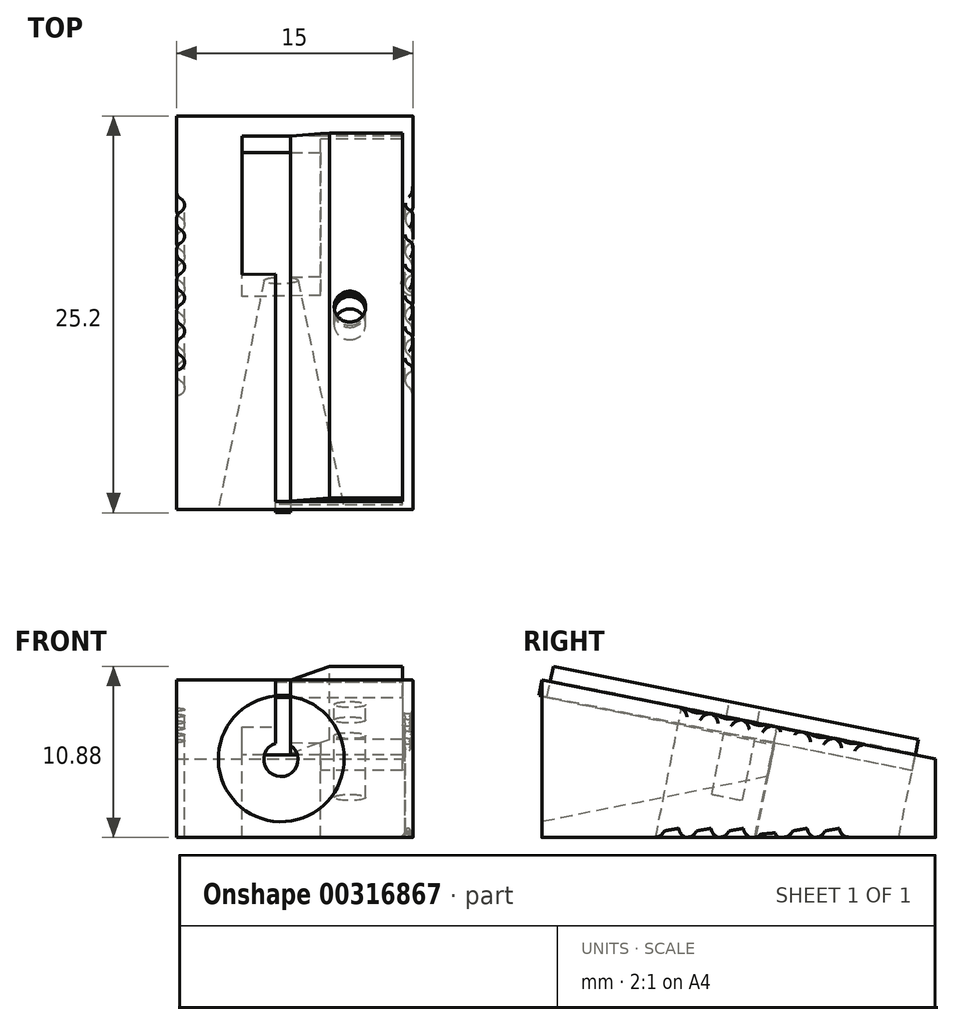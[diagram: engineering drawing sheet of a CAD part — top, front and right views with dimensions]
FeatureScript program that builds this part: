
annotation { "Feature Type Name" : "Feature", "Feature Type Description" : "" }
export const myFeature = defineFeature(function(context is Context, id is Id, definition is map)
    precondition{}
    {
        {
            var Q0;
            Q0=qCreatedBy(makeId("Front.planeOp"),FACE);
            cPlane(context, id + "F0", {"entities" : qUnion([Q0]), "cplaneType" : CPlaneType.OFFSET, "offset" : 10 * mm, "width" : 150 * mm, "height" : 150 * mm});
        }
        {
            var Q0;
            Q0=qCreatedBy(makeId("Front.planeOp"),FACE);
            var sketch = newSketch(context, id + "F1", { "sketchPlane" : qUnion([Q0])});
            skLineSegment(sketch, "E0.bottom", {"start": v(7.5, 5) * mm, "end": v(-7.5, 5) * mm});
            skLineSegment(sketch, "E0.top", {"start": v(7.5, -5) * mm, "end": v(-7.5, -5) * mm});
            skLineSegment(sketch, "E0.left", {"start": v(7.5, 5) * mm, "end": v(7.5, -5) * mm});
            skLineSegment(sketch, "E0.right", {"start": v(-7.5, 5) * mm, "end": v(-7.5, -5) * mm});
            skPoint(sketch, "E0.middle", {"position": v(0, 0) * mm});
            skSolve(sketch);
        }
        {
            var Q0;
            Q0=makeQuery(id+"F1.imprint","IMPRINT",FACE,{"disambiguationData":[TD([[makeQuery(id+"F1.imprint","IMPRINT",EDGE,{"derivedFrom":sQuery(id+"F1.wireOp",EDGE,"E0.bottom")}),1.0]])]});
            extrude(context, id + "F2", {"entities" : qUnion([Q0]), "depth" : 25 * mm});
        }
        {
            var Q0;
            Q0=makeQuery(id+"F2.opExtrude","SWEPT_FACE",FACE,{"disambiguationData":[OSD([sQuery(id+"F1.wireOp",EDGE,"E0.left")])]});
            var sketch = newSketch(context, id + "F3", { "sketchPlane" : qUnion([Q0])});
            skLineSegment(sketch, "E1", {"start": v(0, -5) * mm, "end": v(0, 0) * mm, "construction": true});
            skLineSegment(sketch, "E2", {"start": v(0, 0) * mm, "end": v(-25, 5) * mm, "construction": true});
            skLineSegment(sketch, "E3", {"start": v(-25, 5) * mm, "end": v(0, 0) * mm});
            skLineSegment(sketch, "E4", {"start": v(0, 0) * mm, "end": v(0, 5) * mm});
            skLineSegment(sketch, "E5", {"start": v(0, 5) * mm, "end": v(-25, 5) * mm});
            skSolve(sketch);
        }
        {
            var Q0;
            Q0 = qSketchRegion(id + "F3", true);
            extrude(context, id + "F4", {"entities" : qUnion([Q0]), "operationType" : NewBodyOperationType.REMOVE, "oppositeDirection" : true, "depth" : 25 * mm});
        }
        {
            var Q0;
            Q0=makeQuery(id+"F2.opExtrude","CAP_FACE",FACE,{"disambiguationData":[OSD([sQuery(id+"F1.wireOp",EDGE,"E0.bottom"),sQuery(id+"F1.wireOp",EDGE,"E0.top"),sQuery(id+"F1.wireOp",EDGE,"E0.left"),sQuery(id+"F1.wireOp",EDGE,"E0.right")])],"isStart":false});
            var sketch = newSketch(context, id + "F5", { "sketchPlane" : qUnion([Q0])});
            skCircle(sketch, "E6", {"center": v(-0.86, 0) * mm, "radius": 4 * mm});
            skSolve(sketch);
        }
        {
            var Q0;
            Q0=qCreatedBy(id+"F0.planeOp",FACE);
            var sketch = newSketch(context, id + "F6", { "sketchPlane" : qUnion([Q0])});
            skCircle(sketch, "E7", {"center": v(-0.87, 0) * mm, "radius": 1 * mm});
            skSolve(sketch);
        }
        {
            var Q0;
            Q0=makeQuery(id+"F4.boolean.opBoolean","COPY",FACE,{"derivedFrom":makeQuery(id+"F4.opExtrude","SWEPT_FACE",FACE,{"disambiguationData":[OSD([sQuery(id+"F3.wireOp",EDGE,"E3")])]})});
            var sketch = newSketch(context, id + "F7", { "sketchPlane" : qUnion([Q0])});
            skLineSegment(sketch, "E8", {"start": v(1.64, -10.2) * mm, "end": v(1.64, -1.3) * mm});
            skLineSegment(sketch, "E9", {"start": v(1.64, -1.3) * mm, "end": v(-3.36, -1.3) * mm});
            skLineSegment(sketch, "E10", {"start": v(-3.36, -1.3) * mm, "end": v(-3.36, -10.27) * mm});
            skLineSegment(sketch, "E11", {"start": v(-3.36, -10.27) * mm, "end": v(1.64, -10.2) * mm});
            skSolve(sketch);
        }
        {
            var Q1;
            Q1=makeQuery(id+"F5.imprint","IMPRINT",FACE,{"disambiguationData":[TD([[makeQuery(id+"F5.imprint","IMPRINT",EDGE,{"derivedFrom":sQuery(id+"F5.wireOp",EDGE,"E6")}),1.0]])]});
            var Q2;
            Q2=makeQuery(id+"F6.imprint","IMPRINT",FACE,{"disambiguationData":[TD([[makeQuery(id+"F6.imprint","IMPRINT",EDGE,{"derivedFrom":sQuery(id+"F6.wireOp",EDGE,"E7")}),1.0]])]});
            loft(context, id + "F8", {"operationType" : NewBodyOperationType.REMOVE, "sheetProfilesArray" : [{ "sheetProfileEntities" : qUnion([Q1]) }, { "sheetProfileEntities" : qUnion([Q2]) }]});
        }
        {
            var Q0;
            Q0=makeQuery(id+"F7.imprint","IMPRINT",FACE,{"disambiguationData":[TD([[makeQuery(id+"F7.imprint","IMPRINT",EDGE,{"derivedFrom":sQuery(id+"F7.wireOp",EDGE,"E8")}),1.0]])]});
            extrude(context, id + "F9", {"entities" : qUnion([Q0]), "operationType" : NewBodyOperationType.REMOVE, "oppositeDirection" : true, "depth" : 25 * mm});
        }
        {
            var Q0;
            Q0=qCreatedBy(makeId("Top.planeOp"),FACE);
            var sketch = newSketch(context, id + "F10", { "sketchPlane" : qUnion([Q0])});
            skLineSegment(sketch, "E12.bottom", {"start": v(-0.26, -10.02) * mm, "end": v(-1.23, -10.02) * mm});
            skLineSegment(sketch, "E12.top", {"start": v(-0.26, -26.35) * mm, "end": v(-1.23, -26.35) * mm});
            skLineSegment(sketch, "E12.left", {"start": v(-0.26, -10.02) * mm, "end": v(-0.26, -26.35) * mm});
            skLineSegment(sketch, "E12.right", {"start": v(-1.23, -10.02) * mm, "end": v(-1.23, -26.35) * mm});
            skSolve(sketch);
        }
        {
            var Q0;
            Q0=makeQuery(id+"F10.imprint","IMPRINT",FACE,{"disambiguationData":[TD([[makeQuery(id+"F10.imprint","IMPRINT",EDGE,{"derivedFrom":sQuery(id+"F10.wireOp",EDGE,"E12.bottom")}),1.0]])]});
            extrude(context, id + "F11", {"entities" : qUnion([Q0]), "operationType" : NewBodyOperationType.REMOVE, "depth" : 25 * mm});
        }
        {
            var Q0;
            Q0=makeQuery(id+"F4.boolean.opBoolean","COPY",FACE,{"derivedFrom":makeQuery(id+"F4.opExtrude","SWEPT_FACE",FACE,{"disambiguationData":[OSD([sQuery(id+"F3.wireOp",EDGE,"E3")])]})});
            var sketch = newSketch(context, id + "F12", { "sketchPlane" : qUnion([Q0])});
            skPoint(sketch, "E13.endSnap0", {"position": v(7.5, -12.75) * mm});
            skCircle(sketch, "E14", {"center": v(3.5, -12.5) * mm, "radius": 1 * mm});
            skSolve(sketch);
        }
        {
            var Q0;
            Q0=makeQuery(id+"F12.imprint","IMPRINT",FACE,{"disambiguationData":[TD([[makeQuery(id+"F12.imprint","IMPRINT",EDGE,{"derivedFrom":sQuery(id+"F12.wireOp",EDGE,"E14")}),1.0]])]});
            var Q1;
            Q1=sQuery(id+"F12.wireOp",EDGE,"E14");
            extrude(context, id + "F13", {"entities" : qUnion([Q0]), "operationType" : NewBodyOperationType.REMOVE, "surfaceEntities" : qUnion([Q1]), "oppositeDirection" : true, "depth" : 5 * mm});
        }
        {
            var Q0;
            Q0=makeQuery(id+"F4.boolean.opBoolean","COPY",FACE,{"derivedFrom":makeQuery(id+"F4.opExtrude","SWEPT_FACE",FACE,{"disambiguationData":[OSD([sQuery(id+"F3.wireOp",EDGE,"E3")])]})});
            var sketch = newSketch(context, id + "F14", { "sketchPlane" : qUnion([Q0])});
            skLineSegment(sketch, "E15", {"start": v(-0.26, -24.96) * mm, "end": v(6.83, -24.96) * mm});
            skLineSegment(sketch, "E16", {"start": v(6.83, -24.96) * mm, "end": v(6.83, -1.3) * mm});
            skLineSegment(sketch, "E17", {"start": v(6.83, -1.3) * mm, "end": v(1.64, -1.3) * mm});
            skLineSegment(sketch, "E18", {"start": v(1.64, -1.3) * mm, "end": v(1.64, -10.2) * mm});
            skLineSegment(sketch, "E19", {"start": v(1.64, -10.2) * mm, "end": v(-0.26, -10.23) * mm});
            skLineSegment(sketch, "E20", {"start": v(-0.26, -10.23) * mm, "end": v(-0.26, -24.96) * mm});
            skSolve(sketch);
        }
        {
            var Q0;
            Q0=makeQuery(id+"F14.imprint","IMPRINT",FACE,{"disambiguationData":[TD([[makeQuery(id+"F14.imprint","IMPRINT",EDGE,{"derivedFrom":sQuery(id+"F14.wireOp",EDGE,"E15")}),1.0]])]});
            extrude(context, id + "F15", {"entities" : qUnion([Q0]), "operationType" : NewBodyOperationType.REMOVE, "oppositeDirection" : true, "depth" : 1 * mm});
        }
        {
            var Q0;
            Q0=makeQuery(id+"F4.boolean.opBoolean","COPY",FACE,{"derivedFrom":makeQuery(id+"F4.opExtrude","SWEPT_FACE",FACE,{"disambiguationData":[OSD([sQuery(id+"F3.wireOp",EDGE,"E3")])]})});
            var sketch = newSketch(context, id + "F16", { "sketchPlane" : qUnion([Q0])});
            skLineSegment(sketch, "E21", {"start": v(-0.26, -24.96) * mm, "end": v(-1.23, -24.96) * mm});
            skLineSegment(sketch, "E22", {"start": v(-1.23, -24.96) * mm, "end": v(-1.23, -25.5) * mm});
            skLineSegment(sketch, "E23", {"start": v(-1.23, -25.5) * mm, "end": v(-0.26, -25.5) * mm});
            skLineSegment(sketch, "E24", {"start": v(-0.26, -25.5) * mm, "end": v(-0.26, -24.96) * mm});
            skSolve(sketch);
        }
        {
            var Q0;
            Q0=makeQuery(id+"F16.imprint","IMPRINT",FACE,{"disambiguationData":[TD([[makeQuery(id+"F16.imprint","IMPRINT",EDGE,{"derivedFrom":sQuery(id+"F16.wireOp",EDGE,"E21")}),1.0]])]});
            extrude(context, id + "F17", {"entities" : qUnion([Q0]), "operationType" : NewBodyOperationType.ADD, "oppositeDirection" : true, "depth" : 1 * mm});
        }
        {
            var Q0;
            Q0=makeQuery(id+"F17.boolean.opBoolean","MERGE",FACE,{"derivedFrom":[makeQuery(id+"F4.boolean.opBoolean","COPY",FACE,{"derivedFrom":makeQuery(id+"F4.opExtrude","SWEPT_FACE",FACE,{"disambiguationData":[OSD([sQuery(id+"F3.wireOp",EDGE,"E3")])]})}),makeQuery(id+"F17.opExtrude","CAP_FACE",FACE,{"disambiguationData":[OSD([sQuery(id+"F16.wireOp",EDGE,"E21"),sQuery(id+"F16.wireOp",EDGE,"E22"),sQuery(id+"F16.wireOp",EDGE,"E23"),sQuery(id+"F16.wireOp",EDGE,"E24")])],"isStart":true})]});
            var sketch = newSketch(context, id + "F18", { "sketchPlane" : qUnion([Q0])});
            skLineSegment(sketch, "E25.bottom", {"start": v(6.83, -1.3) * mm, "end": v(-0.27, -1.3) * mm});
            skLineSegment(sketch, "E25.top", {"start": v(6.83, -24.96) * mm, "end": v(-0.27, -24.96) * mm});
            skLineSegment(sketch, "E25.left", {"start": v(6.83, -1.3) * mm, "end": v(6.83, -24.96) * mm});
            skLineSegment(sketch, "E25.right", {"start": v(-0.27, -1.3) * mm, "end": v(-0.27, -24.96) * mm});
            skSolve(sketch);
        }
        {
            var Q0;
            {var subQ1=sQuery(id+"F18.wireOp",EDGE,"E25.top");Q0=makeQuery(id+"F18.imprint","IMPRINT",FACE,{"disambiguationData":[TD([[makeQuery(id+"F18.imprint","IMPRINT",EDGE,{"derivedFrom":subQ1}),1.0]])]});}
            extrude(context, id + "F19", {"entities" : qUnion([Q0]), "depth" : 1 * mm});
        }
        {
            var Q0;
            Q0=makeQuery(id+"F19.opExtrude","CAP_FACE",FACE,{"disambiguationData":[OSD([sQuery(id+"F7.wireOp",EDGE,"E9"),sQuery(id+"F14.wireOp",EDGE,"E17"),sQuery(id+"F18.wireOp",EDGE,"E25.top"),sQuery(id+"F18.wireOp",EDGE,"E25.left"),sQuery(id+"F18.wireOp",EDGE,"E25.right")])],"isStart":false});
            var sketch = newSketch(context, id + "F20", { "sketchPlane" : qUnion([Q0])});
            skCircle(sketch, "E26", {"center": v(3.5, -12.55) * mm, "radius": 1 * mm});
            skSolve(sketch);
        }
        {
            var Q0;
            Q0 = qSketchRegion(id + "F20", true);
            var Q1;
            Q1=sQuery(id+"F20.wireOp",EDGE,"E26");
            extrude(context, id + "F21", {"entities" : qUnion([Q0]), "operationType" : NewBodyOperationType.REMOVE, "surfaceEntities" : qUnion([Q1]), "oppositeDirection" : true, "depth" : 1 * mm});
        }
        {
            var Q0;
            Q0=makeQuery(id+"F19.opExtrude","CAP_EDGE",EDGE,{"disambiguationData":[OSD([sQuery(id+"F18.wireOp",EDGE,"E25.right")])],"isStart":false});
            chamfer(context, id + "F22", {"entities" : qUnion([Q0]), "chamferType" : ChamferType.OFFSET_ANGLE, "width" : 0.9 * mm, "oppositeDirection" : true, "angle" : 70 * degree});
        }
        {
            var Q0;
            {var subQ12=sQuery(id+"F18.wireOp",EDGE,"E25.bottom");Q0=makeQuery(id+"F18.imprint","IMPRINT",FACE,{"disambiguationData":[TD([[makeQuery(id+"F18.imprint","IMPRINT",EDGE,{"derivedFrom":subQ12}),-1.0]])]});}
            var sketch = newSketch(context, id + "F23", { "sketchPlane" : qUnion([Q0])});
            skLineSegment(sketch, "E27", {"start": v(-7.5, -4.67) * mm, "end": v(-7.5, -19.77) * mm});
            skArc(sketch, "E28", {"start": v(-7.5, -6.28) * mm, "mid": v(-7, -5.78) * mm, "end": v(-7.5, -5.28) * mm});
            skArc(sketch, "E29", {"start": v(-7.5, -6.28) * mm, "mid": v(-8, -6.78) * mm, "end": v(-7.5, -7.28) * mm});
            skArc(sketch, "E30", {"start": v(-7.5, -8.29) * mm, "mid": v(-7, -7.79) * mm, "end": v(-7.5, -7.29) * mm});
            skArc(sketch, "E31", {"start": v(-7.5, -8.3) * mm, "mid": v(-8, -8.8) * mm, "end": v(-7.5, -9.3) * mm});
            skArc(sketch, "E32", {"start": v(-7.5, -10.27) * mm, "mid": v(-7, -9.77) * mm, "end": v(-7.5, -9.27) * mm});
            skArc(sketch, "E33", {"start": v(-7.5, -10.28) * mm, "mid": v(-8, -10.78) * mm, "end": v(-7.5, -11.28) * mm});
            skArc(sketch, "E34", {"start": v(-7.5, -12.28) * mm, "mid": v(-7, -11.78) * mm, "end": v(-7.5, -11.28) * mm});
            skArc(sketch, "E35", {"start": v(-7.5, -12.29) * mm, "mid": v(-8, -12.79) * mm, "end": v(-7.5, -13.29) * mm});
            skArc(sketch, "E36", {"start": v(-7.5, -14.44) * mm, "mid": v(-7, -13.94) * mm, "end": v(-7.5, -13.44) * mm});
            skArc(sketch, "E37", {"start": v(-7.5, -14.45) * mm, "mid": v(-8, -14.95) * mm, "end": v(-7.5, -15.45) * mm});
            skArc(sketch, "E38", {"start": v(-7.5, -16.45) * mm, "mid": v(-7, -15.95) * mm, "end": v(-7.5, -15.45) * mm});
            skArc(sketch, "E39", {"start": v(-7.5, -16.46) * mm, "mid": v(-8, -16.96) * mm, "end": v(-7.5, -17.46) * mm});
            skSolve(sketch);
        }
        {
            var Q0;
            Q0 = qSketchRegion(id + "F23", true);
            extrude(context, id + "F24", {"entities" : qUnion([Q0]), "operationType" : NewBodyOperationType.REMOVE, "oppositeDirection" : true, "depth" : 25 * mm});
        }
        {
            var Q0;
            {var subQ12=sQuery(id+"F18.wireOp",EDGE,"E25.bottom");Q0=makeQuery(id+"F18.imprint","IMPRINT",FACE,{"disambiguationData":[TD([[makeQuery(id+"F18.imprint","IMPRINT",EDGE,{"derivedFrom":subQ12}),-1.0]])]});}
            var sketch = newSketch(context, id + "F25", { "sketchPlane" : qUnion([Q0])});
            skLineSegment(sketch, "E40", {"start": v(-7.65, -16.68) * mm, "end": v(7.4, -16.68) * mm, "construction": true});
            skLineSegment(sketch, "E41", {"start": v(7.5, -5.06) * mm, "end": v(7.5, -16.68) * mm});
            skArc(sketch, "E42", {"start": v(7.5, -5.06) * mm, "mid": v(7.02, -5.56) * mm, "end": v(7.5, -6.06) * mm});
            skArc(sketch, "E43", {"start": v(7.5, -7.06) * mm, "mid": v(8, -6.56) * mm, "end": v(7.5, -6.06) * mm});
            skArc(sketch, "E44", {"start": v(7.5, -7.07) * mm, "mid": v(7, -7.57) * mm, "end": v(7.5, -8.07) * mm});
            skArc(sketch, "E45", {"start": v(7.5, -9.02) * mm, "mid": v(8, -8.52) * mm, "end": v(7.5, -8.02) * mm});
            skArc(sketch, "E46", {"start": v(7.5, -9.03) * mm, "mid": v(7, -9.53) * mm, "end": v(7.5, -10.03) * mm});
            skArc(sketch, "E47", {"start": v(7.5, -11.03) * mm, "mid": v(8, -10.53) * mm, "end": v(7.5, -10.03) * mm});
            skArc(sketch, "E48", {"start": v(7.5, -11.04) * mm, "mid": v(7, -11.54) * mm, "end": v(7.5, -12.04) * mm});
            skArc(sketch, "E49", {"start": v(7.5, -13.05) * mm, "mid": v(8, -12.55) * mm, "end": v(7.5, -12.05) * mm});
            skArc(sketch, "E50", {"start": v(7.5, -13.05) * mm, "mid": v(7, -13.55) * mm, "end": v(7.5, -14.05) * mm});
            skArc(sketch, "E51", {"start": v(7.5, -15.06) * mm, "mid": v(8, -14.56) * mm, "end": v(7.5, -14.06) * mm});
            skArc(sketch, "E52", {"start": v(7.5, -15.06) * mm, "mid": v(7, -15.56) * mm, "end": v(7.5, -16.06) * mm});
            skSolve(sketch);
        }
        {
            var Q0;
            Q0=makeQuery(id+"FrYQUd1mb8N4bva_2.boolean.opBoolean","SPLIT",FACE,{"disambiguationData":[TD([makeQuery(id+"F2.opExtrude","SWEPT_FACE",FACE,{"disambiguationData":[OSD([sQuery(id+"F1.wireOp",EDGE,"E0.top")])]}),makeQuery(id+"F4.boolean.opBoolean","COPY",FACE,{"derivedFrom":makeQuery(id+"F4.opExtrude","SWEPT_FACE",FACE,{"disambiguationData":[OSD([sQuery(id+"F3.wireOp",EDGE,"E3")])]})}),makeQuery(id+"F17.opExtrude","CAP_FACE",FACE,{"disambiguationData":[OSD([sQuery(id+"F16.wireOp",EDGE,"E21"),sQuery(id+"F16.wireOp",EDGE,"E22"),sQuery(id+"F16.wireOp",EDGE,"E23"),sQuery(id+"F16.wireOp",EDGE,"E24")])],"isStart":true}),makeQuery(id+"FrYQUd1mb8N4bva_2.opExtrude","SWEPT_FACE",FACE,{"disambiguationData":[OSD([sQuery(id+"F25.wireOp",EDGE,"E44")])]}),makeQuery(id+"FrYQUd1mb8N4bva_2.opExtrude","SWEPT_FACE",FACE,{"disambiguationData":[OSD([sQuery(id+"F25.wireOp",EDGE,"E46")])]})])],"derivedFrom":makeQuery(id+"F2.opExtrude","SWEPT_FACE",FACE,{"disambiguationData":[OSD([sQuery(id+"F1.wireOp",EDGE,"E0.left")])]})});
            var Q1;
            Q1=makeQuery(id+"FrYQUd1mb8N4bva_2.boolean.opBoolean","SPLIT",FACE,{"disambiguationData":[TD([makeQuery(id+"F2.opExtrude","SWEPT_FACE",FACE,{"disambiguationData":[OSD([sQuery(id+"F1.wireOp",EDGE,"E0.top")])]}),makeQuery(id+"F4.boolean.opBoolean","COPY",FACE,{"derivedFrom":makeQuery(id+"F4.opExtrude","SWEPT_FACE",FACE,{"disambiguationData":[OSD([sQuery(id+"F3.wireOp",EDGE,"E3")])]})}),makeQuery(id+"F17.opExtrude","CAP_FACE",FACE,{"disambiguationData":[OSD([sQuery(id+"F16.wireOp",EDGE,"E21"),sQuery(id+"F16.wireOp",EDGE,"E22"),sQuery(id+"F16.wireOp",EDGE,"E23"),sQuery(id+"F16.wireOp",EDGE,"E24")])],"isStart":true}),makeQuery(id+"FrYQUd1mb8N4bva_2.opExtrude","SWEPT_FACE",FACE,{"disambiguationData":[OSD([sQuery(id+"F25.wireOp",EDGE,"E46")])]}),makeQuery(id+"FrYQUd1mb8N4bva_2.opExtrude","SWEPT_FACE",FACE,{"disambiguationData":[OSD([sQuery(id+"F25.wireOp",EDGE,"E48")])]})])],"derivedFrom":makeQuery(id+"F2.opExtrude","SWEPT_FACE",FACE,{"disambiguationData":[OSD([sQuery(id+"F1.wireOp",EDGE,"E0.left")])]})});
            var Q2;
            Q2=makeQuery(id+"FrYQUd1mb8N4bva_2.boolean.opBoolean","SPLIT",FACE,{"disambiguationData":[TD([makeQuery(id+"F2.opExtrude","SWEPT_FACE",FACE,{"disambiguationData":[OSD([sQuery(id+"F1.wireOp",EDGE,"E0.top")])]}),makeQuery(id+"F4.boolean.opBoolean","COPY",FACE,{"derivedFrom":makeQuery(id+"F4.opExtrude","SWEPT_FACE",FACE,{"disambiguationData":[OSD([sQuery(id+"F3.wireOp",EDGE,"E3")])]})}),makeQuery(id+"F17.opExtrude","CAP_FACE",FACE,{"disambiguationData":[OSD([sQuery(id+"F16.wireOp",EDGE,"E21"),sQuery(id+"F16.wireOp",EDGE,"E22"),sQuery(id+"F16.wireOp",EDGE,"E23"),sQuery(id+"F16.wireOp",EDGE,"E24")])],"isStart":true}),makeQuery(id+"FrYQUd1mb8N4bva_2.opExtrude","SWEPT_FACE",FACE,{"disambiguationData":[OSD([sQuery(id+"F25.wireOp",EDGE,"E48")])]}),makeQuery(id+"FrYQUd1mb8N4bva_2.opExtrude","SWEPT_FACE",FACE,{"disambiguationData":[OSD([sQuery(id+"F25.wireOp",EDGE,"E50")])]})])],"derivedFrom":makeQuery(id+"F2.opExtrude","SWEPT_FACE",FACE,{"disambiguationData":[OSD([sQuery(id+"F1.wireOp",EDGE,"E0.left")])]})});
            var Q3;
            Q3=makeQuery(id+"FrYQUd1mb8N4bva_2.boolean.opBoolean","SPLIT",FACE,{"disambiguationData":[TD([makeQuery(id+"F2.opExtrude","SWEPT_FACE",FACE,{"disambiguationData":[OSD([sQuery(id+"F1.wireOp",EDGE,"E0.top")])]}),makeQuery(id+"F4.boolean.opBoolean","COPY",FACE,{"derivedFrom":makeQuery(id+"F4.opExtrude","SWEPT_FACE",FACE,{"disambiguationData":[OSD([sQuery(id+"F3.wireOp",EDGE,"E3")])]})}),makeQuery(id+"F17.opExtrude","CAP_FACE",FACE,{"disambiguationData":[OSD([sQuery(id+"F16.wireOp",EDGE,"E21"),sQuery(id+"F16.wireOp",EDGE,"E22"),sQuery(id+"F16.wireOp",EDGE,"E23"),sQuery(id+"F16.wireOp",EDGE,"E24")])],"isStart":true}),makeQuery(id+"FrYQUd1mb8N4bva_2.opExtrude","SWEPT_FACE",FACE,{"disambiguationData":[OSD([sQuery(id+"F25.wireOp",EDGE,"E50")])]}),makeQuery(id+"FrYQUd1mb8N4bva_2.opExtrude","SWEPT_FACE",FACE,{"disambiguationData":[OSD([sQuery(id+"F25.wireOp",EDGE,"E52")])]})])],"derivedFrom":makeQuery(id+"F2.opExtrude","SWEPT_FACE",FACE,{"disambiguationData":[OSD([sQuery(id+"F1.wireOp",EDGE,"E0.left")])]})});
            fillet(context, id + "F26", {"entities" : qUnion([Q0, Q1, Q2, Q3]), "radius" : 0.02 * mm, "tangentPropagation" : true, "allowEdgeOverflow" : false});
        }
        {
            var Q0;
            Q0 = qSketchRegion(id + "F25", true);
            extrude(context, id + "F27", {"entities" : qUnion([Q0]), "operationType" : NewBodyOperationType.REMOVE, "oppositeDirection" : true, "depth" : 25 * mm});
        }
        {
            var Q0;
            Q0=makeQuery(id+"F27.boolean.opBoolean","COPY",EDGE,{"derivedFrom":makeQuery(id+"F27.opExtrude","SWEPT_EDGE",EDGE,{"disambiguationData":[OSD([sQuery(id+"F3.wireOp",EDGE,"E3"),sQuery(id+"F25.wireOp",EDGE,"E41"),sQuery(id+"F25.wireOp",EDGE,"E42")])]})});
            var Q1;
            Q1=makeQuery(id+"F27.boolean.opBoolean","COPY",EDGE,{"derivedFrom":makeQuery(id+"F27.opExtrude","SWEPT_EDGE",EDGE,{"disambiguationData":[OSD([sQuery(id+"F25.wireOp",EDGE,"E41"),sQuery(id+"F25.wireOp",EDGE,"E42")])]})});
            var Q2;
            {var subQ0=sQuery(id+"F25.wireOp",EDGE,"E44");var subQ1=sQuery(id+"F25.wireOp",EDGE,"E41");Q2=makeQuery(id+"F27.boolean.opBoolean","COPY",EDGE,{"derivedFrom":makeQuery(id+"F27.opExtrude","SWEPT_EDGE",EDGE,{"disambiguationData":[OSD([subQ1,subQ0]),TDD([makeQuery(id+"F25.imprint","INTERSECT",VERTEX,{"disambiguationData":[OD(0.0)],"derivedFrom":[subQ1,subQ0]})])]})});}
            var Q3;
            {var subQ0=sQuery(id+"F25.wireOp",EDGE,"E44");var subQ1=sQuery(id+"F25.wireOp",EDGE,"E41");Q3=makeQuery(id+"F27.boolean.opBoolean","COPY",EDGE,{"derivedFrom":makeQuery(id+"F27.opExtrude","SWEPT_EDGE",EDGE,{"disambiguationData":[OSD([subQ1,subQ0]),TDD([makeQuery(id+"F25.imprint","INTERSECT",VERTEX,{"disambiguationData":[OD(1.0)],"derivedFrom":[subQ1,subQ0]})])]})});}
            var Q4;
            {var subQ0=sQuery(id+"F25.wireOp",EDGE,"E52");var subQ1=sQuery(id+"F25.wireOp",EDGE,"E41");Q4=makeQuery(id+"F27.boolean.opBoolean","COPY",EDGE,{"derivedFrom":makeQuery(id+"F27.opExtrude","SWEPT_EDGE",EDGE,{"disambiguationData":[OSD([subQ1,subQ0]),TDD([makeQuery(id+"F25.imprint","INTERSECT",VERTEX,{"disambiguationData":[OD(1.0)],"derivedFrom":[subQ1,subQ0]})])]})});}
            var Q5;
            {var subQ0=sQuery(id+"F25.wireOp",EDGE,"E50");var subQ1=sQuery(id+"F25.wireOp",EDGE,"E41");Q5=makeQuery(id+"F27.boolean.opBoolean","COPY",EDGE,{"derivedFrom":makeQuery(id+"F27.opExtrude","SWEPT_EDGE",EDGE,{"disambiguationData":[OSD([subQ1,subQ0]),TDD([makeQuery(id+"F25.imprint","INTERSECT",VERTEX,{"disambiguationData":[OD(1.0)],"derivedFrom":[subQ1,subQ0]})])]})});}
            var Q6;
            {var subQ0=sQuery(id+"F25.wireOp",EDGE,"E50");var subQ1=sQuery(id+"F25.wireOp",EDGE,"E41");Q6=makeQuery(id+"F27.boolean.opBoolean","COPY",EDGE,{"derivedFrom":makeQuery(id+"F27.opExtrude","SWEPT_EDGE",EDGE,{"disambiguationData":[OSD([subQ1,subQ0]),TDD([makeQuery(id+"F25.imprint","INTERSECT",VERTEX,{"disambiguationData":[OD(0.0)],"derivedFrom":[subQ1,subQ0]})])]})});}
            var Q7;
            {var subQ0=sQuery(id+"F25.wireOp",EDGE,"E48");var subQ1=sQuery(id+"F25.wireOp",EDGE,"E41");Q7=makeQuery(id+"F27.boolean.opBoolean","COPY",EDGE,{"derivedFrom":makeQuery(id+"F27.opExtrude","SWEPT_EDGE",EDGE,{"disambiguationData":[OSD([subQ1,subQ0]),TDD([makeQuery(id+"F25.imprint","INTERSECT",VERTEX,{"disambiguationData":[OD(1.0)],"derivedFrom":[subQ1,subQ0]})])]})});}
            var Q8;
            {var subQ0=sQuery(id+"F25.wireOp",EDGE,"E48");var subQ1=sQuery(id+"F25.wireOp",EDGE,"E41");Q8=makeQuery(id+"F27.boolean.opBoolean","COPY",EDGE,{"derivedFrom":makeQuery(id+"F27.opExtrude","SWEPT_EDGE",EDGE,{"disambiguationData":[OSD([subQ1,subQ0]),TDD([makeQuery(id+"F25.imprint","INTERSECT",VERTEX,{"disambiguationData":[OD(0.0)],"derivedFrom":[subQ1,subQ0]})])]})});}
            fillet(context, id + "F28", {"entities" : qUnion([Q0, Q1, Q2, Q3, Q4, Q5, Q6, Q7, Q8]), "radius" : 0.5 * mm, "tangentPropagation" : true, "allowEdgeOverflow" : false});
        }
        {
            var Q0;
            {var subQ0=sQuery(id+"F25.wireOp",EDGE,"E46");var subQ1=sQuery(id+"F25.wireOp",EDGE,"E41");Q0=makeQuery(id+"F27.boolean.opBoolean","COPY",EDGE,{"derivedFrom":makeQuery(id+"F27.opExtrude","SWEPT_EDGE",EDGE,{"disambiguationData":[OSD([subQ1,subQ0]),TDD([makeQuery(id+"F25.imprint","INTERSECT",VERTEX,{"disambiguationData":[OD(0.0)],"derivedFrom":[subQ1,subQ0]})])]})});}
            var Q1;
            {var subQ0=sQuery(id+"F25.wireOp",EDGE,"E46");var subQ1=sQuery(id+"F25.wireOp",EDGE,"E41");Q1=makeQuery(id+"F27.boolean.opBoolean","COPY",EDGE,{"derivedFrom":makeQuery(id+"F27.opExtrude","SWEPT_EDGE",EDGE,{"disambiguationData":[OSD([subQ1,subQ0]),TDD([makeQuery(id+"F25.imprint","INTERSECT",VERTEX,{"disambiguationData":[OD(1.0)],"derivedFrom":[subQ1,subQ0]})])]})});}
            fillet(context, id + "F29", {"entities" : qUnion([Q0, Q1]), "radius" : 0.25 * mm, "tangentPropagation" : true, "allowEdgeOverflow" : false});
        }
        {
            var Q0;
            {var subQ0=sQuery(id+"F23.wireOp",EDGE,"E28");var subQ1=sQuery(id+"F23.wireOp",EDGE,"E27");Q0=makeQuery(id+"F24.boolean.opBoolean","COPY",EDGE,{"derivedFrom":makeQuery(id+"F24.opExtrude","SWEPT_EDGE",EDGE,{"disambiguationData":[OSD([subQ1,subQ0]),TDD([makeQuery(id+"F23.imprint","INTERSECT",VERTEX,{"disambiguationData":[OD(1.0)],"derivedFrom":[subQ1,subQ0]})])]})});}
            var Q1;
            {var subQ0=sQuery(id+"F23.wireOp",EDGE,"E28");var subQ1=sQuery(id+"F23.wireOp",EDGE,"E27");Q1=makeQuery(id+"F24.boolean.opBoolean","COPY",EDGE,{"derivedFrom":makeQuery(id+"F24.opExtrude","SWEPT_EDGE",EDGE,{"disambiguationData":[OSD([subQ1,subQ0]),TDD([makeQuery(id+"F23.imprint","INTERSECT",VERTEX,{"disambiguationData":[OD(0.0)],"derivedFrom":[subQ1,subQ0]})])]})});}
            var Q2;
            {var subQ0=sQuery(id+"F23.wireOp",EDGE,"E30");var subQ1=sQuery(id+"F23.wireOp",EDGE,"E27");Q2=makeQuery(id+"F24.boolean.opBoolean","COPY",EDGE,{"derivedFrom":makeQuery(id+"F24.opExtrude","SWEPT_EDGE",EDGE,{"disambiguationData":[OSD([subQ1,subQ0]),TDD([makeQuery(id+"F23.imprint","INTERSECT",VERTEX,{"disambiguationData":[OD(1.0)],"derivedFrom":[subQ1,subQ0]})])]})});}
            var Q3;
            {var subQ0=sQuery(id+"F23.wireOp",EDGE,"E30");var subQ1=sQuery(id+"F23.wireOp",EDGE,"E27");Q3=makeQuery(id+"F24.boolean.opBoolean","COPY",EDGE,{"derivedFrom":makeQuery(id+"F24.opExtrude","SWEPT_EDGE",EDGE,{"disambiguationData":[OSD([subQ1,subQ0]),TDD([makeQuery(id+"F23.imprint","INTERSECT",VERTEX,{"disambiguationData":[OD(0.0)],"derivedFrom":[subQ1,subQ0]})])]})});}
            var Q4;
            {var subQ0=sQuery(id+"F23.wireOp",EDGE,"E32");var subQ1=sQuery(id+"F23.wireOp",EDGE,"E27");Q4=makeQuery(id+"F24.boolean.opBoolean","COPY",EDGE,{"derivedFrom":makeQuery(id+"F24.opExtrude","SWEPT_EDGE",EDGE,{"disambiguationData":[OSD([subQ1,subQ0]),TDD([makeQuery(id+"F23.imprint","INTERSECT",VERTEX,{"disambiguationData":[OD(1.0)],"derivedFrom":[subQ1,subQ0]})])]})});}
            var Q5;
            {var subQ0=sQuery(id+"F23.wireOp",EDGE,"E32");var subQ1=sQuery(id+"F23.wireOp",EDGE,"E27");Q5=makeQuery(id+"F24.boolean.opBoolean","COPY",EDGE,{"derivedFrom":makeQuery(id+"F24.opExtrude","SWEPT_EDGE",EDGE,{"disambiguationData":[OSD([subQ1,subQ0]),TDD([makeQuery(id+"F23.imprint","INTERSECT",VERTEX,{"disambiguationData":[OD(0.0)],"derivedFrom":[subQ1,subQ0]})])]})});}
            var Q6;
            {var subQ0=sQuery(id+"F23.wireOp",EDGE,"E34");var subQ1=sQuery(id+"F23.wireOp",EDGE,"E27");Q6=makeQuery(id+"F24.boolean.opBoolean","COPY",EDGE,{"derivedFrom":makeQuery(id+"F24.opExtrude","SWEPT_EDGE",EDGE,{"disambiguationData":[OSD([subQ1,subQ0]),TDD([makeQuery(id+"F23.imprint","INTERSECT",VERTEX,{"disambiguationData":[OD(1.0)],"derivedFrom":[subQ1,subQ0]})])]})});}
            var Q7;
            {var subQ0=sQuery(id+"F23.wireOp",EDGE,"E34");var subQ1=sQuery(id+"F23.wireOp",EDGE,"E27");Q7=makeQuery(id+"F24.boolean.opBoolean","COPY",EDGE,{"derivedFrom":makeQuery(id+"F24.opExtrude","SWEPT_EDGE",EDGE,{"disambiguationData":[OSD([subQ1,subQ0]),TDD([makeQuery(id+"F23.imprint","INTERSECT",VERTEX,{"disambiguationData":[OD(0.0)],"derivedFrom":[subQ1,subQ0]})])]})});}
            var Q8;
            {var subQ0=sQuery(id+"F23.wireOp",EDGE,"E36");var subQ1=sQuery(id+"F23.wireOp",EDGE,"E27");Q8=makeQuery(id+"F24.boolean.opBoolean","COPY",EDGE,{"derivedFrom":makeQuery(id+"F24.opExtrude","SWEPT_EDGE",EDGE,{"disambiguationData":[OSD([subQ1,subQ0]),TDD([makeQuery(id+"F23.imprint","INTERSECT",VERTEX,{"disambiguationData":[OD(1.0)],"derivedFrom":[subQ1,subQ0]})])]})});}
            var Q9;
            {var subQ0=sQuery(id+"F23.wireOp",EDGE,"E36");var subQ1=sQuery(id+"F23.wireOp",EDGE,"E27");Q9=makeQuery(id+"F24.boolean.opBoolean","COPY",EDGE,{"derivedFrom":makeQuery(id+"F24.opExtrude","SWEPT_EDGE",EDGE,{"disambiguationData":[OSD([subQ1,subQ0]),TDD([makeQuery(id+"F23.imprint","INTERSECT",VERTEX,{"disambiguationData":[OD(0.0)],"derivedFrom":[subQ1,subQ0]})])]})});}
            var Q10;
            {var subQ0=sQuery(id+"F23.wireOp",EDGE,"E38");var subQ1=sQuery(id+"F23.wireOp",EDGE,"E27");Q10=makeQuery(id+"F24.boolean.opBoolean","COPY",EDGE,{"derivedFrom":makeQuery(id+"F24.opExtrude","SWEPT_EDGE",EDGE,{"disambiguationData":[OSD([subQ1,subQ0]),TDD([makeQuery(id+"F23.imprint","INTERSECT",VERTEX,{"disambiguationData":[OD(1.0)],"derivedFrom":[subQ1,subQ0]})])]})});}
            var Q11;
            {var subQ0=sQuery(id+"F23.wireOp",EDGE,"E38");var subQ1=sQuery(id+"F23.wireOp",EDGE,"E27");Q11=makeQuery(id+"F24.boolean.opBoolean","COPY",EDGE,{"derivedFrom":makeQuery(id+"F24.opExtrude","SWEPT_EDGE",EDGE,{"disambiguationData":[OSD([subQ1,subQ0]),TDD([makeQuery(id+"F23.imprint","INTERSECT",VERTEX,{"disambiguationData":[OD(0.0)],"derivedFrom":[subQ1,subQ0]})])]})});}
            fillet(context, id + "F30", {"entities" : qUnion([Q0, Q1, Q2, Q3, Q4, Q5, Q6, Q7, Q8, Q9, Q10, Q11]), "radius" : 0.5 * mm, "tangentPropagation" : true, "allowEdgeOverflow" : false});
        }
    });
